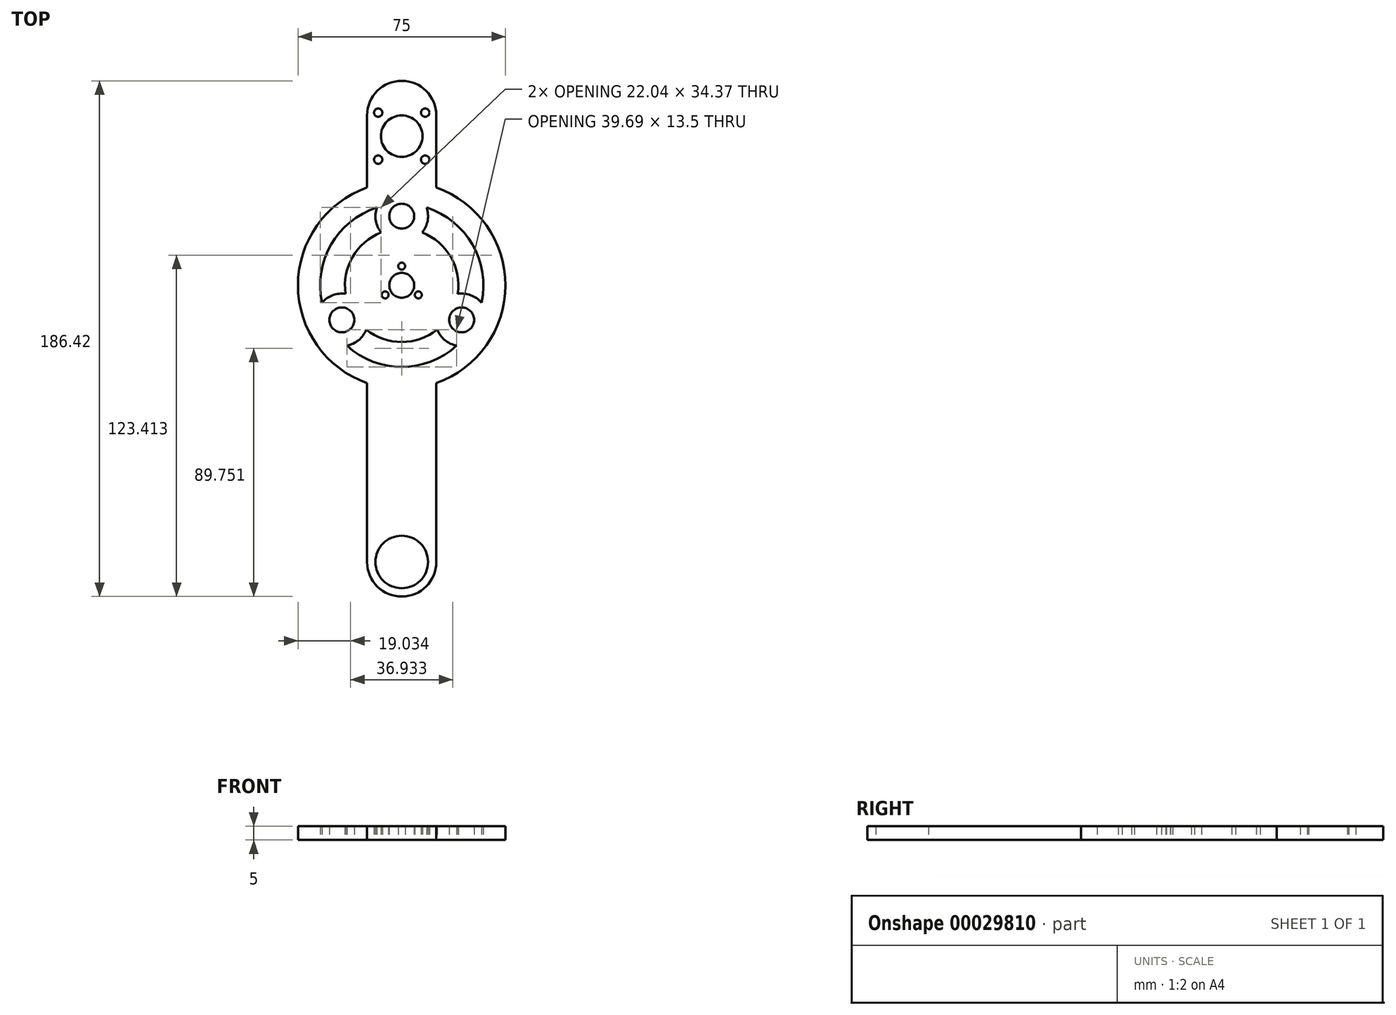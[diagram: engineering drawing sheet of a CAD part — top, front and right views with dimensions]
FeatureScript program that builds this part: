
annotation { "Feature Type Name" : "Feature", "Feature Type Description" : "" }
export const myFeature = defineFeature(function(context is Context, id is Id, definition is map)
    precondition{}
    {
        {
            var Q0;
            Q0=qCreatedBy(makeId("Top.planeOp"),FACE);
            var sketch = newSketch(context, id + "F0", { "sketchPlane" : qUnion([Q0])});
            skCircle(sketch, "E0", {"center": v(0, 0) * mm, "radius": 37.5 * mm});
            skLineSegment(sketch, "E1", {"start": v(-12.5, 35.36) * mm, "end": v(-12.5, 61.42) * mm});
            skArc(sketch, "E2", {"start": v(12.5, 61.42) * mm, "mid": v(0, 73.92) * mm, "end": v(-12.5, 61.42) * mm});
            skLineSegment(sketch, "E3", {"start": v(12.5, 61.42) * mm, "end": v(12.5, 35.36) * mm});
            skLineSegment(sketch, "E4", {"start": v(-12.5, -35.36) * mm, "end": v(-12.5, -100) * mm});
            skArc(sketch, "E5", {"start": v(-12.5, -100) * mm, "mid": v(0, -112.5) * mm, "end": v(12.5, -100) * mm});
            skLineSegment(sketch, "E6", {"start": v(12.5, -100) * mm, "end": v(12.5, -35.36) * mm});
            skCircle(sketch, "E7", {"center": v(-8.5, 45.42) * mm, "radius": 1.5 * mm});
            skCircle(sketch, "E8", {"center": v(8.5, 45.42) * mm, "radius": 1.5 * mm});
            skCircle(sketch, "E9", {"center": v(0, 53.92) * mm, "radius": 7.5 * mm});
            skCircle(sketch, "E10", {"center": v(8.5, 62.42) * mm, "radius": 1.5 * mm});
            skLineSegment(sketch, "E11", {"start": v(8.5, 45.42) * mm, "end": v(0, 53.92) * mm, "construction": true});
            skCircle(sketch, "E12", {"center": v(-8.5, 62.42) * mm, "radius": 1.5 * mm});
            skLineSegment(sketch, "E13", {"start": v(-8.5, 45.42) * mm, "end": v(0, 53.92) * mm, "construction": true});
            skLineSegment(sketch, "E14", {"start": v(-8.5, 62.42) * mm, "end": v(0, 53.92) * mm, "construction": true});
            skLineSegment(sketch, "E15", {"start": v(-12.5, 35.36) * mm, "end": v(12.5, 35.36) * mm, "construction": true});
            skLineSegment(sketch, "E16", {"start": v(12.5, -35.36) * mm, "end": v(-12.5, -35.36) * mm, "construction": true});
            skLineSegment(sketch, "E17", {"start": v(0, 0) * mm, "end": v(0, -18.97) * mm, "construction": true});
            skCircle(sketch, "E18", {"center": v(0, 0) * mm, "radius": 4.5 * mm});
            skLineSegment(sketch, "E19", {"start": v(8.5, 62.42) * mm, "end": v(0, 53.92) * mm, "construction": true});
            skCircle(sketch, "E20", {"center": v(0, -100) * mm, "radius": 9.5 * mm});
            skCircle(sketch, "E21", {"center": v(0, 6.93) * mm, "radius": 1.25 * mm});
            skCircle(sketch, "E22", {"center": v(6, -3.46) * mm, "radius": 1.25 * mm});
            skCircle(sketch, "E23", {"center": v(-6, -3.46) * mm, "radius": 1.25 * mm});
            skCircle(sketch, "E24", {"center": v(0, 0) * mm, "radius": 10 * mm});
            skLineSegment(sketch, "E25", {"start": v(-6, -3.46) * mm, "end": v(0, 6.93) * mm, "construction": true});
            skLineSegment(sketch, "E26", {"start": v(6, -3.46) * mm, "end": v(0, 6.93) * mm, "construction": true});
            skLineSegment(sketch, "E27", {"start": v(-6, -3.46) * mm, "end": v(6, -3.46) * mm, "construction": true});
            skLineSegment(sketch, "E28", {"start": v(-6, -3.46) * mm, "end": v(0, 0) * mm, "construction": true});
            skLineSegment(sketch, "E29", {"start": v(0, 6.93) * mm, "end": v(0, 0) * mm, "construction": true});
            skLineSegment(sketch, "E30", {"start": v(0, 0) * mm, "end": v(6, -3.46) * mm, "construction": true});
            skCircle(sketch, "E31", {"center": v(0, 25) * mm, "radius": 4.5 * mm});
            skCircle(sketch, "E32", {"center": v(21.65, -12.5) * mm, "radius": 4.5 * mm});
            skCircle(sketch, "E33", {"center": v(-21.65, -12.5) * mm, "radius": 4.5 * mm});
            skLineSegment(sketch, "E34", {"start": v(0, 25) * mm, "end": v(0, 6.93) * mm, "construction": true});
            skLineSegment(sketch, "E35", {"start": v(-21.65, -12.5) * mm, "end": v(-6, -3.46) * mm, "construction": true});
            skLineSegment(sketch, "E36", {"start": v(21.65, -12.5) * mm, "end": v(6, -3.46) * mm, "construction": true});
            skCircle(sketch, "E37", {"center": v(0, 25) * mm, "radius": 9.5 * mm});
            skCircle(sketch, "E38", {"center": v(-21.65, -12.5) * mm, "radius": 9.5 * mm});
            skCircle(sketch, "E39", {"center": v(21.65, -12.5) * mm, "radius": 9.5 * mm});
            skCircle(sketch, "E40", {"center": v(0, 0) * mm, "radius": 20.5 * mm});
            skCircle(sketch, "E41", {"center": v(0, 0) * mm, "radius": 29.5 * mm});
            skSolve(sketch);
        }
        {
            var Q0;
            Q0 = qSketchRegion(id + "F0", true);
            var Q1;
            {var subQ0=sQuery(id+"F0.wireOp",EDGE,"55e76af4-ff7d-4902-8194-23b5d1213256");var subQ2=sQuery(id+"F0.wireOp",EDGE,"25387a36-7e12-4ac9-bd1b-64446be451f5");var subQ4=makeQuery(id+"F0.imprint","INTERSECT",VERTEX,{"disambiguationData":[OD(0.0)],"derivedFrom":[subQ2,subQ0]});Q1=makeQuery(id+"F0.imprint","IMPRINT",FACE,{"disambiguationData":[TD([[makeQuery(id+"F0.imprint","IMPRINT",EDGE,{"disambiguationData":[TD([[subQ4,-1.0]])],"derivedFrom":subQ2}),1.0]])]});}
            var Q2;
            Q2=makeQuery(id+"F0.imprint","IMPRINT",FACE,{"disambiguationData":[TD([[makeQuery(id+"F0.imprint","IMPRINT",EDGE,{"derivedFrom":sQuery(id+"F0.wireOp",EDGE,"E18")}),-1.0]])]});
            var Q3;
            {var subQ0=sQuery(id+"F0.wireOp",EDGE,"55e76af4-ff7d-4902-8194-23b5d1213256");var subQ3=sQuery(id+"F0.wireOp",EDGE,"25387a36-7e12-4ac9-bd1b-64446be451f5");var subQ4=makeQuery(id+"F0.imprint","INTERSECT",VERTEX,{"disambiguationData":[OD(0.0)],"derivedFrom":[subQ3,subQ0]});Q3=makeQuery(id+"F0.imprint","IMPRINT",FACE,{"disambiguationData":[TD([[makeQuery(id+"F0.imprint","IMPRINT",EDGE,{"disambiguationData":[TD([[subQ4,1.0]])],"derivedFrom":subQ3}),1.0]])]});}
            var Q4;
            {var subQ0=sQuery(id+"F0.wireOp",EDGE,"dd525a7c-7dce-4a06-8177-d9d2553b9335");var subQ2=sQuery(id+"F0.wireOp",EDGE,"25387a36-7e12-4ac9-bd1b-64446be451f5");var subQ4=makeQuery(id+"F0.imprint","INTERSECT",VERTEX,{"disambiguationData":[OD(0.0)],"derivedFrom":[subQ2,subQ0]});Q4=makeQuery(id+"F0.imprint","IMPRINT",FACE,{"disambiguationData":[TD([[makeQuery(id+"F0.imprint","IMPRINT",EDGE,{"disambiguationData":[TD([[subQ4,1.0]])],"derivedFrom":subQ2}),1.0]])]});}
            var Q5;
            {var subQ0=sQuery(id+"F0.wireOp",EDGE,"55e76af4-ff7d-4902-8194-23b5d1213256");var subQ3=sQuery(id+"F0.wireOp",EDGE,"25387a36-7e12-4ac9-bd1b-64446be451f5");var subQ4=makeQuery(id+"F0.imprint","INTERSECT",VERTEX,{"disambiguationData":[OD(1.0)],"derivedFrom":[subQ3,subQ0]});Q5=makeQuery(id+"F0.imprint","IMPRINT",FACE,{"disambiguationData":[TD([[makeQuery(id+"F0.imprint","IMPRINT",EDGE,{"disambiguationData":[TD([[subQ4,-1.0]])],"derivedFrom":subQ3}),1.0]])]});}
            var Q6;
            {var subQ3=sQuery(id+"F0.wireOp",EDGE,"b7f10987-ea30-4f7d-9cbb-5c5b287627f4");var subQ5=sQuery(id+"F0.wireOp",EDGE,"dd525a7c-7dce-4a06-8177-d9d2553b9335");var subQ7=makeQuery(id+"F0.imprint","INTERSECT",VERTEX,{"disambiguationData":[OD(0.0)],"derivedFrom":[subQ3,subQ5]});Q6=makeQuery(id+"F0.imprint","IMPRINT",FACE,{"disambiguationData":[TD([[makeQuery(id+"F0.imprint","IMPRINT",EDGE,{"disambiguationData":[TD([[subQ7,1.0]])],"derivedFrom":subQ3}),1.0]])]});}
            var Q7;
            {var subQ0=sQuery(id+"F0.wireOp",EDGE,"55e76af4-ff7d-4902-8194-23b5d1213256");var subQ2=sQuery(id+"F0.wireOp",EDGE,"b7f10987-ea30-4f7d-9cbb-5c5b287627f4");var subQ3=makeQuery(id+"F0.imprint","INTERSECT",VERTEX,{"disambiguationData":[OD(0.0)],"derivedFrom":[subQ2,subQ0]});Q7=makeQuery(id+"F0.imprint","IMPRINT",FACE,{"disambiguationData":[TD([[makeQuery(id+"F0.imprint","IMPRINT",EDGE,{"disambiguationData":[TD([[subQ3,1.0]])],"derivedFrom":subQ2}),1.0]])]});}
            var Q8;
            {var subQ3=sQuery(id+"F0.wireOp",EDGE,"b7f10987-ea30-4f7d-9cbb-5c5b287627f4");var subQ5=sQuery(id+"F0.wireOp",EDGE,"dd525a7c-7dce-4a06-8177-d9d2553b9335");var subQ7=makeQuery(id+"F0.imprint","INTERSECT",VERTEX,{"disambiguationData":[OD(1.0)],"derivedFrom":[subQ3,subQ5]});Q8=makeQuery(id+"F0.imprint","IMPRINT",FACE,{"disambiguationData":[TD([[makeQuery(id+"F0.imprint","IMPRINT",EDGE,{"disambiguationData":[TD([[subQ7,-1.0]])],"derivedFrom":subQ3}),1.0]])]});}
            var Q9;
            {var subQ0=sQuery(id+"F0.wireOp",EDGE,"dd525a7c-7dce-4a06-8177-d9d2553b9335");var subQ2=sQuery(id+"F0.wireOp",EDGE,"b7f10987-ea30-4f7d-9cbb-5c5b287627f4");var subQ3=makeQuery(id+"F0.imprint","INTERSECT",VERTEX,{"disambiguationData":[OD(0.0)],"derivedFrom":[subQ2,subQ0]});Q9=makeQuery(id+"F0.imprint","IMPRINT",FACE,{"disambiguationData":[TD([[makeQuery(id+"F0.imprint","IMPRINT",EDGE,{"disambiguationData":[TD([[subQ3,-1.0]])],"derivedFrom":subQ2}),1.0]])]});}
            var Q10;
            {var subQ3=sQuery(id+"F0.wireOp",EDGE,"a940a7dc-2615-4278-8fdb-ebe8dec3286c");var subQ5=sQuery(id+"F0.wireOp",EDGE,"dd525a7c-7dce-4a06-8177-d9d2553b9335");var subQ7=makeQuery(id+"F0.imprint","INTERSECT",VERTEX,{"disambiguationData":[OD(1.0)],"derivedFrom":[subQ3,subQ5]});Q10=makeQuery(id+"F0.imprint","IMPRINT",FACE,{"disambiguationData":[TD([[makeQuery(id+"F0.imprint","IMPRINT",EDGE,{"disambiguationData":[TD([[subQ7,1.0]])],"derivedFrom":subQ3}),1.0]])]});}
            var Q11;
            {var subQ0=sQuery(id+"F0.wireOp",EDGE,"dd525a7c-7dce-4a06-8177-d9d2553b9335");var subQ2=sQuery(id+"F0.wireOp",EDGE,"a940a7dc-2615-4278-8fdb-ebe8dec3286c");var subQ4=makeQuery(id+"F0.imprint","INTERSECT",VERTEX,{"disambiguationData":[OD(0.0)],"derivedFrom":[subQ2,subQ0]});Q11=makeQuery(id+"F0.imprint","IMPRINT",FACE,{"disambiguationData":[TD([[makeQuery(id+"F0.imprint","IMPRINT",EDGE,{"disambiguationData":[TD([[subQ4,1.0]])],"derivedFrom":subQ2}),1.0]])]});}
            var Q12;
            {var subQ3=sQuery(id+"F0.wireOp",EDGE,"a940a7dc-2615-4278-8fdb-ebe8dec3286c");var subQ5=sQuery(id+"F0.wireOp",EDGE,"dd525a7c-7dce-4a06-8177-d9d2553b9335");var subQ7=makeQuery(id+"F0.imprint","INTERSECT",VERTEX,{"disambiguationData":[OD(0.0)],"derivedFrom":[subQ3,subQ5]});Q12=makeQuery(id+"F0.imprint","IMPRINT",FACE,{"disambiguationData":[TD([[makeQuery(id+"F0.imprint","IMPRINT",EDGE,{"disambiguationData":[TD([[subQ7,-1.0]])],"derivedFrom":subQ3}),1.0]])]});}
            var Q13;
            {var subQ0=sQuery(id+"F0.wireOp",EDGE,"55e76af4-ff7d-4902-8194-23b5d1213256");var subQ2=sQuery(id+"F0.wireOp",EDGE,"a940a7dc-2615-4278-8fdb-ebe8dec3286c");var subQ4=makeQuery(id+"F0.imprint","INTERSECT",VERTEX,{"disambiguationData":[OD(0.0)],"derivedFrom":[subQ2,subQ0]});Q13=makeQuery(id+"F0.imprint","IMPRINT",FACE,{"disambiguationData":[TD([[makeQuery(id+"F0.imprint","IMPRINT",EDGE,{"disambiguationData":[TD([[subQ4,-1.0]])],"derivedFrom":subQ2}),1.0]])]});}
            var Q14;
            {var subQ0=sQuery(id+"F0.wireOp",EDGE,"E41");var subQ1=sQuery(id+"F0.wireOp",EDGE,"E38");var subQ4=makeQuery(id+"F0.imprint","INTERSECT",VERTEX,{"disambiguationData":[OD(0.0)],"derivedFrom":[subQ1,subQ0]});Q14=makeQuery(id+"F0.imprint","IMPRINT",FACE,{"disambiguationData":[TD([[makeQuery(id+"F0.imprint","IMPRINT",EDGE,{"disambiguationData":[TD([[subQ4,-1.0]])],"derivedFrom":subQ1}),1.0]])]});}
            var Q15;
            {var subQ0=sQuery(id+"F0.wireOp",EDGE,"E40");var subQ1=sQuery(id+"F0.wireOp",EDGE,"E38");var subQ4=makeQuery(id+"F0.imprint","INTERSECT",VERTEX,{"disambiguationData":[OD(0.0)],"derivedFrom":[subQ1,subQ0]});Q15=makeQuery(id+"F0.imprint","IMPRINT",FACE,{"disambiguationData":[TD([[makeQuery(id+"F0.imprint","IMPRINT",EDGE,{"disambiguationData":[TD([[subQ4,1.0]])],"derivedFrom":subQ1}),1.0]])]});}
            var Q16;
            {var subQ3=sQuery(id+"F0.wireOp",EDGE,"E33");var subQ5=sQuery(id+"F0.wireOp",EDGE,"E40");var subQ7=makeQuery(id+"F0.imprint","INTERSECT",VERTEX,{"derivedFrom":[subQ3,subQ5]});Q16=makeQuery(id+"F0.imprint","IMPRINT",FACE,{"disambiguationData":[TD([[makeQuery(id+"F0.imprint","IMPRINT",EDGE,{"disambiguationData":[TD([[subQ7,1.0]])],"derivedFrom":subQ3}),-1.0]])]});}
            var Q17;
            {var subQ3=sQuery(id+"F0.wireOp",EDGE,"E33");var subQ5=sQuery(id+"F0.wireOp",EDGE,"E40");var subQ7=makeQuery(id+"F0.imprint","INTERSECT",VERTEX,{"derivedFrom":[subQ3,subQ5]});Q17=makeQuery(id+"F0.imprint","IMPRINT",FACE,{"disambiguationData":[TD([[makeQuery(id+"F0.imprint","IMPRINT",EDGE,{"disambiguationData":[TD([[subQ7,-1.0]])],"derivedFrom":subQ3}),-1.0]])]});}
            var Q18;
            {var subQ3=sQuery(id+"F0.wireOp",EDGE,"E32");var subQ5=sQuery(id+"F0.wireOp",EDGE,"E40");var subQ7=makeQuery(id+"F0.imprint","INTERSECT",VERTEX,{"derivedFrom":[subQ3,subQ5]});Q18=makeQuery(id+"F0.imprint","IMPRINT",FACE,{"disambiguationData":[TD([[makeQuery(id+"F0.imprint","IMPRINT",EDGE,{"disambiguationData":[TD([[subQ7,-1.0]])],"derivedFrom":subQ3}),-1.0]])]});}
            var Q19;
            {var subQ3=sQuery(id+"F0.wireOp",EDGE,"E32");var subQ5=sQuery(id+"F0.wireOp",EDGE,"E40");var subQ7=makeQuery(id+"F0.imprint","INTERSECT",VERTEX,{"derivedFrom":[subQ3,subQ5]});Q19=makeQuery(id+"F0.imprint","IMPRINT",FACE,{"disambiguationData":[TD([[makeQuery(id+"F0.imprint","IMPRINT",EDGE,{"disambiguationData":[TD([[subQ7,1.0]])],"derivedFrom":subQ3}),-1.0]])]});}
            var Q20;
            {var subQ0=sQuery(id+"F0.wireOp",EDGE,"E40");var subQ1=sQuery(id+"F0.wireOp",EDGE,"E39");var subQ2=makeQuery(id+"F0.imprint","INTERSECT",VERTEX,{"disambiguationData":[OD(0.0)],"derivedFrom":[subQ1,subQ0]});Q20=makeQuery(id+"F0.imprint","IMPRINT",FACE,{"disambiguationData":[TD([[makeQuery(id+"F0.imprint","IMPRINT",EDGE,{"disambiguationData":[TD([[subQ2,-1.0]])],"derivedFrom":subQ1}),1.0]])]});}
            var Q21;
            {var subQ0=sQuery(id+"F0.wireOp",EDGE,"E41");var subQ1=sQuery(id+"F0.wireOp",EDGE,"E39");var subQ2=makeQuery(id+"F0.imprint","INTERSECT",VERTEX,{"disambiguationData":[OD(0.0)],"derivedFrom":[subQ1,subQ0]});Q21=makeQuery(id+"F0.imprint","IMPRINT",FACE,{"disambiguationData":[TD([[makeQuery(id+"F0.imprint","IMPRINT",EDGE,{"disambiguationData":[TD([[subQ2,1.0]])],"derivedFrom":subQ1}),1.0]])]});}
            var Q22;
            {var subQ0=sQuery(id+"F0.wireOp",EDGE,"E40");var subQ1=sQuery(id+"F0.wireOp",EDGE,"E37");var subQ2=makeQuery(id+"F0.imprint","INTERSECT",VERTEX,{"disambiguationData":[OD(0.0)],"derivedFrom":[subQ1,subQ0]});Q22=makeQuery(id+"F0.imprint","IMPRINT",FACE,{"disambiguationData":[TD([[makeQuery(id+"F0.imprint","IMPRINT",EDGE,{"disambiguationData":[TD([[subQ2,-1.0]])],"derivedFrom":subQ1}),1.0]])]});}
            var Q23;
            {var subQ3=sQuery(id+"F0.wireOp",EDGE,"E31");var subQ5=sQuery(id+"F0.wireOp",EDGE,"E40");var subQ7=makeQuery(id+"F0.imprint","INTERSECT",VERTEX,{"derivedFrom":[subQ3,subQ5]});Q23=makeQuery(id+"F0.imprint","IMPRINT",FACE,{"disambiguationData":[TD([[makeQuery(id+"F0.imprint","IMPRINT",EDGE,{"disambiguationData":[TD([[subQ7,-1.0]])],"derivedFrom":subQ3}),-1.0]])]});}
            var Q24;
            {var subQ0=sQuery(id+"F0.wireOp",EDGE,"E41");var subQ1=sQuery(id+"F0.wireOp",EDGE,"E37");var subQ2=makeQuery(id+"F0.imprint","INTERSECT",VERTEX,{"disambiguationData":[OD(0.0)],"derivedFrom":[subQ1,subQ0]});Q24=makeQuery(id+"F0.imprint","IMPRINT",FACE,{"disambiguationData":[TD([[makeQuery(id+"F0.imprint","IMPRINT",EDGE,{"disambiguationData":[TD([[subQ2,1.0]])],"derivedFrom":subQ1}),1.0]])]});}
            var Q25;
            {var subQ3=sQuery(id+"F0.wireOp",EDGE,"E31");var subQ5=sQuery(id+"F0.wireOp",EDGE,"E40");var subQ7=makeQuery(id+"F0.imprint","INTERSECT",VERTEX,{"derivedFrom":[subQ3,subQ5]});Q25=makeQuery(id+"F0.imprint","IMPRINT",FACE,{"disambiguationData":[TD([[makeQuery(id+"F0.imprint","IMPRINT",EDGE,{"disambiguationData":[TD([[subQ7,1.0]])],"derivedFrom":subQ3}),-1.0]])]});}
            var Q26;
            Q26=makeQuery(id+"F0.imprint","IMPRINT",FACE,{"disambiguationData":[TD([[makeQuery(id+"F0.imprint","IMPRINT",EDGE,{"derivedFrom":sQuery(id+"F0.wireOp",EDGE,"E24")}),-1.0]])]});
            extrude(context, id + "F1", {"entities" : qUnion([Q0, Q1, Q2, Q3, Q4, Q5, Q6, Q7, Q8, Q9, Q10, Q11, Q12, Q13, Q14, Q15, Q16, Q17, Q18, Q19, Q20, Q21, Q22, Q23, Q24, Q25, Q26]), "depth" : 5 * mm});
        }
    });
